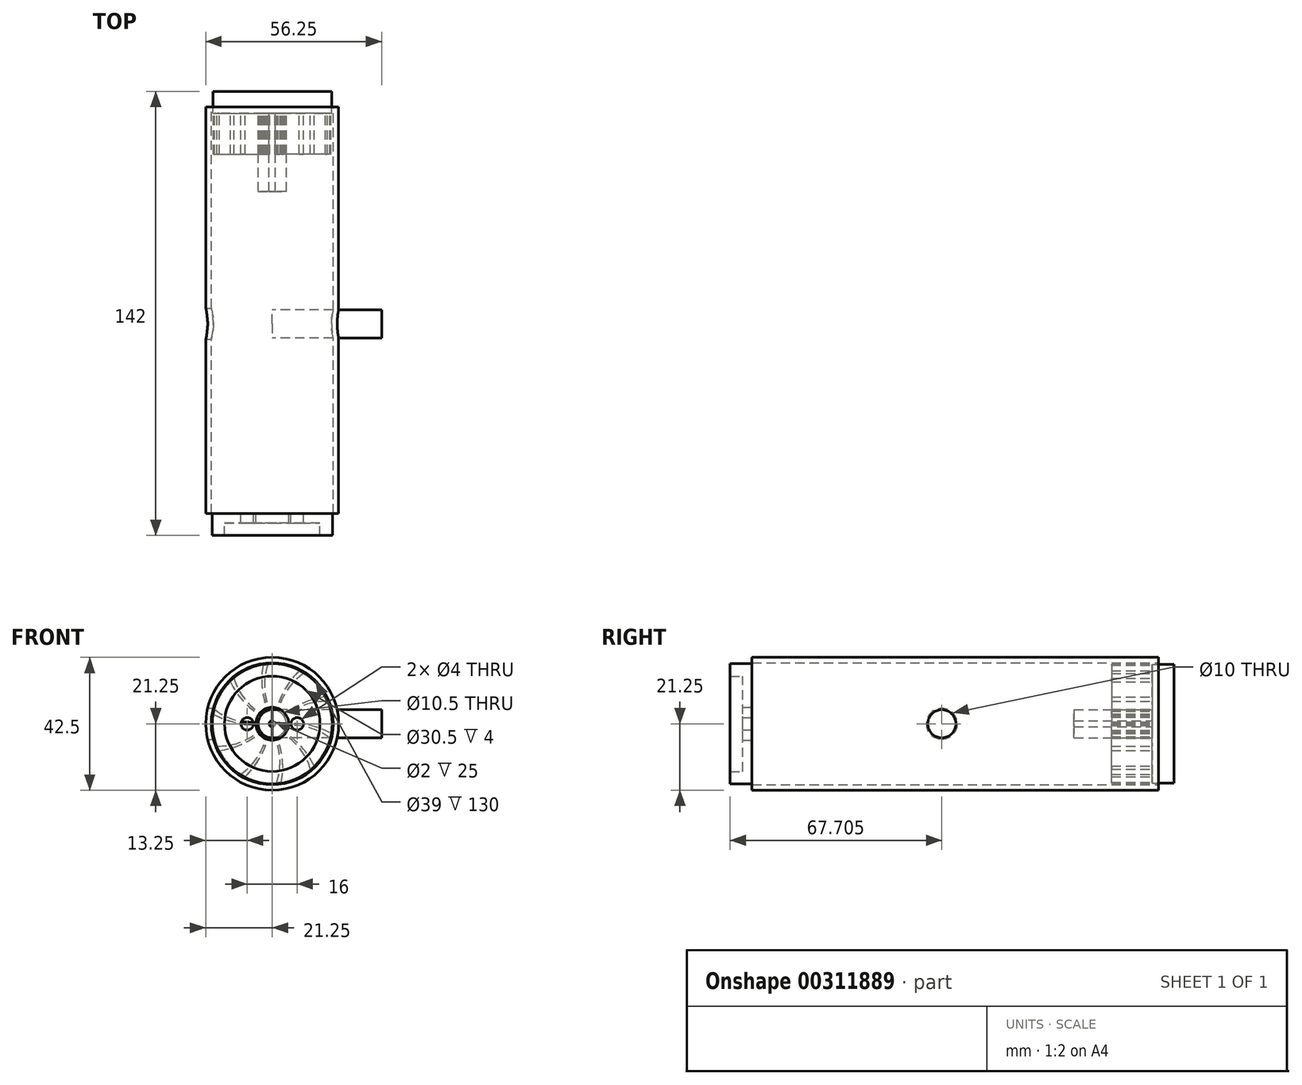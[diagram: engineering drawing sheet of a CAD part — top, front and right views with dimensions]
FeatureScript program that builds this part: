
annotation { "Feature Type Name" : "Feature", "Feature Type Description" : "" }
export const myFeature = defineFeature(function(context is Context, id is Id, definition is map)
    precondition{}
    {
        {
            var Q0;
            Q0=qCreatedBy(makeId("Front.planeOp"),FACE);
            var sketch = newSketch(context, id + "F0", { "sketchPlane" : qUnion([Q0])});
            skCircle(sketch, "E0", {"center": v(0, 0) * mm, "radius": 19.5 * mm});
            skCircle(sketch, "E1", {"center": v(0, 0) * mm, "radius": 21.25 * mm});
            skSolve(sketch);
        }
        {
            var Q0;
            Q0=makeQuery(id+"F0.imprint","IMPRINT",FACE,{"disambiguationData":[TD([[makeQuery(id+"F0.imprint","IMPRINT",EDGE,{"derivedFrom":sQuery(id+"F0.wireOp",EDGE,"E0")}),-1.0]])]});
            extrude(context, id + "F1", {"entities" : qUnion([Q0]), "depth" : 130 * mm});
        }
        {
            var Q0;
            Q0=qCreatedBy(makeId("Front.planeOp"),FACE);
            var sketch = newSketch(context, id + "F2", { "sketchPlane" : qUnion([Q0])});
            skCircle(sketch, "E2", {"center": v(0, 0) * mm, "radius": 19 * mm});
            skSolve(sketch);
        }
        {
            var Q0;
            Q0 = qSketchRegion(id + "F2", true);
            extrude(context, id + "F3", {"entities" : qUnion([Q0]), "depth" : 2 * mm});
        }
        {
            var Q0;
            Q0=qCreatedBy(makeId("Right.planeOp"),FACE);
            var sketch = newSketch(context, id + "F4", { "sketchPlane" : qUnion([Q0])});
            skLineSegment(sketch, "E3", {"start": v(0, 0) * mm, "end": v(16.68, 0) * mm, "construction": true});
            skSolve(sketch);
        }
        {
            var Q0;
            Q0=qCreatedBy(makeId("Front.planeOp"),FACE);
            var sketch = newSketch(context, id + "F5", { "sketchPlane" : qUnion([Q0])});
            skCircle(sketch, "E4", {"center": v(0, 0) * mm, "radius": 4 * mm});
            skArc(sketch, "E5", {"start": v(-18.44, 4.58) * mm, "mid": v(-11.58, 1.17) * mm, "end": v(-3.95, 0.65) * mm});
            skArc(sketch, "E6", {"start": v(-18.76, 3.02) * mm, "mid": v(-11.6, 0.4) * mm, "end": v(-4, 0) * mm});
            skArc(sketch, "E7", {"start": v(-18.76, 3.02) * mm, "mid": v(-18.58, 3.8) * mm, "end": v(-18.44, 4.58) * mm});
            skArc(sketch, "E8", {"start": v(-3.95, 0.65) * mm, "mid": v(-4, 0.33) * mm, "end": v(-4, 0) * mm});
            skSolve(sketch);
        }
        {
            var Q0;
            Q0=makeQuery(id+"F5.imprint","IMPRINT",FACE,{"disambiguationData":[TD([[makeQuery(id+"F5.imprint","IMPRINT",EDGE,{"derivedFrom":sQuery(id+"F5.wireOp",EDGE,"E5")}),-1.0]])]});
            var Q1;
            {var subQ0=sQuery(id+"F5.wireOp",EDGE,"E8");Q1=makeQuery(id+"F5.imprint","IMPRINT",FACE,{"disambiguationData":[TD([[makeQuery(id+"F5.imprint","IMPRINT",EDGE,{"derivedFrom":subQ0}),1.0]])]});}
            extrude(context, id + "F6", {"entities" : qUnion([Q0, Q1]), "operationType" : NewBodyOperationType.ADD, "depth" : 15 * mm});
        }
        {
            var Q0;
            Q0=makeQuery(id+"F3.opExtrude","SWEPT_BODY",BODY,{"disambiguationData":[OSD([sQuery(id+"F2.wireOp",EDGE,"E2")])]});
            var Q1;
            Q1=sQuery(id+"F4.wireOp",EDGE,"E3");
            circularPattern(context, id + "F7", {"entities" : qUnion([Q0]), "axis" : qUnion([Q1]), "angle" : 360 * degree, "instanceCount" : 10, "equalSpace" : true});
        }
        {
            var Q0;
            {var subQ0=sQuery(id+"F2.wireOp",EDGE,"E2");var subQ1=makeQuery(id+"F3.opExtrude","CAP_FACE",FACE,{"disambiguationData":[OSD([subQ0])],"isStart":false});Q0=makeQuery(id+"F7.opPattern","COPY",FACE,{"derivedFrom":makeQuery(id+"F6.boolean.opBoolean","SPLIT",FACE,{"disambiguationData":[TD([makeQuery(id+"F3.opExtrude","SWEPT_FACE",FACE,{"disambiguationData":[OSD([subQ0])]}),subQ1,makeQuery(id+"F6.opExtrude","SWEPT_FACE",FACE,{"disambiguationData":[OSD([sQuery(id+"F5.wireOp",EDGE,"E5")])]}),makeQuery(id+"F6.opExtrude","SWEPT_FACE",FACE,{"disambiguationData":[OSD([sQuery(id+"F5.wireOp",EDGE,"E6")])]}),makeQuery(id+"F6.opExtrude","SWEPT_FACE",FACE,{"disambiguationData":[OSD([sQuery(id+"F5.wireOp",EDGE,"E4")])]}),makeQuery(id+"F6.opExtrude","SWEPT_FACE",FACE,{"disambiguationData":[OSD([sQuery(id+"F5.wireOp",EDGE,"E7")])]})])],"derivedFrom":subQ1}),"instanceName":"7"});}
            var sketch = newSketch(context, id + "F8", { "sketchPlane" : qUnion([Q0])});
            skCircle(sketch, "E9", {"center": v(0, 0) * mm, "radius": 1 * mm});
            skCircle(sketch, "E10", {"center": v(0, 0) * mm, "radius": 4.5 * mm});
            skSolve(sketch);
        }
        {
            var Q0;
            Q0 = qSketchRegion(id + "F8", true);
            extrude(context, id + "F9", {"entities" : qUnion([Q0]), "operationType" : NewBodyOperationType.ADD, "depth" : 25 * mm});
        }
        {
            var Q0;
            {var subQ0=makeQuery(id+"F6.opExtrude","SWEPT_FACE",FACE,{"disambiguationData":[OSD([sQuery(id+"F5.wireOp",EDGE,"E5")])]});var subQ1=sQuery(id+"F2.wireOp",EDGE,"E2");var subQ2=makeQuery(id+"F3.opExtrude","CAP_FACE",FACE,{"disambiguationData":[OSD([subQ1])],"isStart":false});var subQ3=makeQuery(id+"F6.opExtrude","SWEPT_FACE",FACE,{"disambiguationData":[OSD([sQuery(id+"F5.wireOp",EDGE,"E7")])]});var subQ4=subQ3;var subQ5=makeQuery(id+"F3.opExtrude","SWEPT_FACE",FACE,{"disambiguationData":[OSD([subQ1])]});var subQ6=makeQuery(id+"F6.opExtrude","SWEPT_FACE",FACE,{"disambiguationData":[OSD([sQuery(id+"F5.wireOp",EDGE,"E6")])]});Q0=makeQuery(id+"F9.boolean.opBoolean","SPLIT",FACE,{"disambiguationData":[TD([subQ5,subQ2,makeQuery(id+"F7.opPattern","COPY",FACE,{"derivedFrom":subQ0,"instanceName":"3"}),makeQuery(id+"F7.opPattern","COPY",FACE,{"derivedFrom":subQ4,"instanceName":"3"}),makeQuery(id+"F7.opPattern","COPY",FACE,{"derivedFrom":subQ6,"instanceName":"4"}),makeQuery(id+"F7.opPattern","COPY",FACE,{"derivedFrom":subQ4,"instanceName":"4"}),makeQuery(id+"F9.opExtrude","SWEPT_FACE",FACE,{"disambiguationData":[OSD([sQuery(id+"F8.wireOp",EDGE,"E10")])]})])],"derivedFrom":makeQuery(id+"F6.boolean.opBoolean","SPLIT",FACE,{"disambiguationData":[TD([subQ5,subQ2,subQ0,subQ6,makeQuery(id+"F6.opExtrude","SWEPT_FACE",FACE,{"disambiguationData":[OSD([sQuery(id+"F5.wireOp",EDGE,"E4")])]}),subQ3])],"derivedFrom":subQ2})});}
            cPlane(context, id + "F10", {"entities" : qUnion([Q0]), "cplaneType" : CPlaneType.OFFSET, "offset" : 30 * mm, "width" : 150 * mm, "height" : 150 * mm});
        }
        {
            var Q0;
            Q0=qCreatedBy(id+"F10.planeOp",FACE);
            var sketch = newSketch(context, id + "F11", { "sketchPlane" : qUnion([Q0])});
            skCircle(sketch, "E11", {"center": v(0, 0) * mm, "radius": 13.5 * mm});
            skCircle(sketch, "E12", {"center": v(0, 0) * mm, "radius": 5 * mm});
            skCircle(sketch, "E13", {"center": v(8, 0) * mm, "radius": 1 * mm});
            skCircle(sketch, "E14", {"center": v(-8, 0) * mm, "radius": 1 * mm});
            skSolve(sketch);
        }
        {
            var Q0;
            Q0=makeQuery(id+"F11.imprint","IMPRINT",FACE,{"disambiguationData":[TD([[makeQuery(id+"F11.imprint","IMPRINT",EDGE,{"derivedFrom":sQuery(id+"F11.wireOp",EDGE,"E11")}),1.0]])]});
            extrude(context, id + "F12", {"entities" : qUnion([Q0]), "depth" : 2 * mm});
        }
        {
            var Q0;
            Q0=makeQuery(id+"F1.opExtrude","CAP_FACE",FACE,{"disambiguationData":[OSD([sQuery(id+"F0.wireOp",EDGE,"E0"),sQuery(id+"F0.wireOp",EDGE,"E1")])],"isStart":true});
            var sketch = newSketch(context, id + "F13", { "sketchPlane" : qUnion([Q0])});
            skCircle(sketch, "E15", {"center": v(0, 0) * mm, "radius": 19 * mm});
            skSolve(sketch);
        }
        {
            var Q0;
            Q0=makeQuery(id+"F13.imprint","IMPRINT",FACE,{"disambiguationData":[TD([[makeQuery(id+"F13.imprint","IMPRINT",EDGE,{"derivedFrom":sQuery(id+"F13.wireOp",EDGE,"E15")}),1.0]])]});
            extrude(context, id + "F14", {"entities" : qUnion([Q0]), "depth" : 5 * mm});
        }
        {
            var Q0;
            Q0=makeQuery(id+"F12.opExtrude","SWEPT_BODY",BODY,{"disambiguationData":[OSD([sQuery(id+"F11.wireOp",EDGE,"E11"),sQuery(id+"F11.wireOp",EDGE,"E12"),sQuery(id+"F11.wireOp",EDGE,"E13"),sQuery(id+"F11.wireOp",EDGE,"E14")])]});
            deleteBodies(context, id + "F15", {"entities" : qUnion([Q0])});
        }
        {
            var Q0;
            Q0=makeQuery(id+"F1.opExtrude","CAP_FACE",FACE,{"disambiguationData":[OSD([sQuery(id+"F0.wireOp",EDGE,"E0"),sQuery(id+"F0.wireOp",EDGE,"E1")])],"isStart":false});
            var sketch = newSketch(context, id + "F16", { "sketchPlane" : qUnion([Q0])});
            skCircle(sketch, "E16", {"center": v(0, 0) * mm, "radius": 19.25 * mm});
            skCircle(sketch, "E17", {"center": v(-8, 0) * mm, "radius": 2 * mm});
            skCircle(sketch, "E18", {"center": v(8, 0) * mm, "radius": 2 * mm});
            skCircle(sketch, "E19", {"center": v(0, 0) * mm, "radius": 5.25 * mm});
            skSolve(sketch);
        }
        {
            var Q0;
            Q0=makeQuery(id+"F16.imprint","IMPRINT",FACE,{"disambiguationData":[TD([[makeQuery(id+"F16.imprint","IMPRINT",EDGE,{"derivedFrom":sQuery(id+"F16.wireOp",EDGE,"E16")}),1.0]])]});
            extrude(context, id + "F17", {"entities" : qUnion([Q0]), "depth" : 3 * mm});
        }
        {
            var Q0;
            Q0=makeQuery(id+"F17.opExtrude","CAP_FACE",FACE,{"disambiguationData":[OSD([sQuery(id+"F16.wireOp",EDGE,"E16"),sQuery(id+"F16.wireOp",EDGE,"E17"),sQuery(id+"F16.wireOp",EDGE,"E18"),sQuery(id+"F16.wireOp",EDGE,"E19")])],"isStart":false});
            var sketch = newSketch(context, id + "F18", { "sketchPlane" : qUnion([Q0])});
            skCircle(sketch, "E20", {"center": v(0, 0) * mm, "radius": 15.25 * mm});
            skCircle(sketch, "E21", {"center": v(0, 0) * mm, "radius": 19.25 * mm});
            skSolve(sketch);
        }
        {
            var Q0;
            Q0=makeQuery(id+"F18.imprint","IMPRINT",FACE,{"disambiguationData":[TD([[makeQuery(id+"F18.imprint","IMPRINT",EDGE,{"derivedFrom":sQuery(id+"F18.wireOp",EDGE,"E20")}),-1.0]])]});
            extrude(context, id + "F19", {"entities" : qUnion([Q0]), "operationType" : NewBodyOperationType.ADD, "depth" : 4 * mm});
        }
        {
            var Q0;
            Q0=qCreatedBy(makeId("Right.planeOp"),FACE);
            var sketch = newSketch(context, id + "F20", { "sketchPlane" : qUnion([Q0])});
            skLineSegment(sketch, "E22", {"start": v(0, 0) * mm, "end": v(-81.47, 0) * mm, "construction": true});
            skCircle(sketch, "E23", {"center": v(-69.3, 0) * mm, "radius": 5 * mm});
            skSolve(sketch);
        }
        {
            var Q0;
            Q0 = qSketchRegion(id + "F20", true);
            extrude(context, id + "F21", {"entities" : qUnion([Q0]), "operationType" : NewBodyOperationType.REMOVE, "oppositeDirection" : true, "depth" : 25 * mm});
        }
        {
            var Q0;
            Q0=qCreatedBy(makeId("Right.planeOp"),FACE);
            var sketch = newSketch(context, id + "F22", { "sketchPlane" : qUnion([Q0])});
            skCircle(sketch, "E24", {"center": v(-69.3, 0) * mm, "radius": 4.5 * mm});
            skSolve(sketch);
        }
        {
            var Q0;
            Q0=qCreatedBy(makeId("Right.planeOp"),FACE);
            var sketch = newSketch(context, id + "F23", { "sketchPlane" : qUnion([Q0])});
            skCircle(sketch, "E25", {"center": v(-69.3, 0) * mm, "radius": 3.5 * mm});
            skCircle(sketch, "E26", {"center": v(-69.3, 0) * mm, "radius": 4.5 * mm});
            skSolve(sketch);
        }
        {
            var Q0;
            Q0 = qSketchRegion(id + "F23", true);
            var Q1;
            Q1=makeQuery(id+"F22.imprint","IMPRINT",FACE,{"disambiguationData":[TD([[makeQuery(id+"F22.imprint","IMPRINT",EDGE,{"derivedFrom":sQuery(id+"F22.wireOp",EDGE,"E24")}),1.0]])]});
            extrude(context, id + "F24", {"entities" : qUnion([Q0, Q1]), "operationType" : NewBodyOperationType.ADD, "depth" : 35 * mm});
        }
    });
